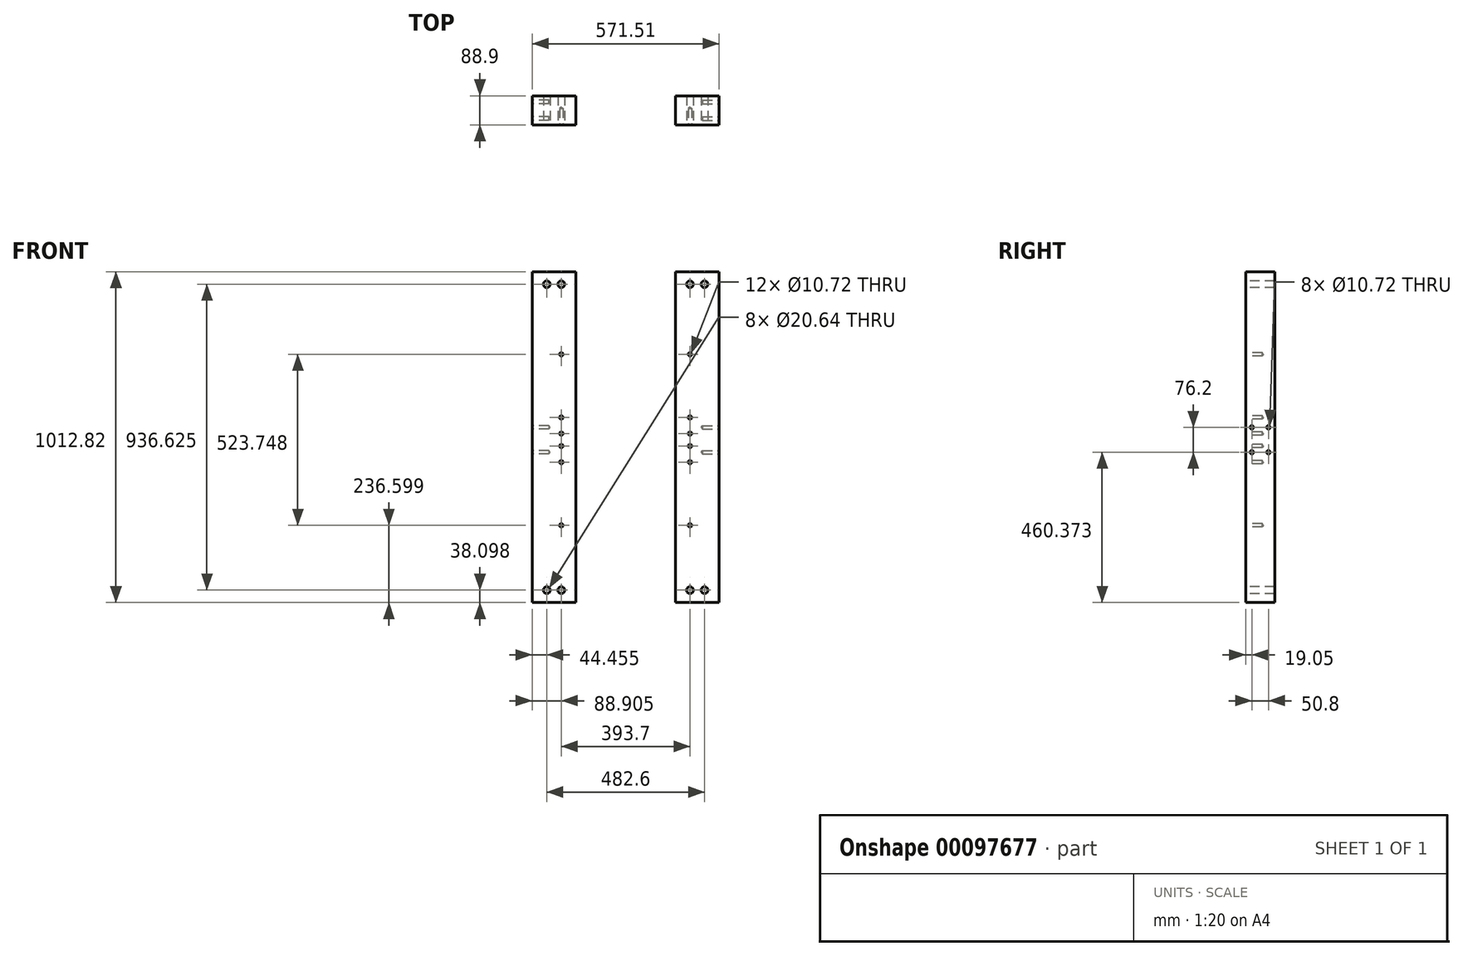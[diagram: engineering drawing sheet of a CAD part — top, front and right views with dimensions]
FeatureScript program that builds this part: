
annotation { "Feature Type Name" : "Feature", "Feature Type Description" : "" }
export const myFeature = defineFeature(function(context is Context, id is Id, definition is map)
    precondition{}
    {
        {
            var Q0;
            Q0=qCreatedBy(makeId("Top.planeOp"),FACE);
            var sketch = newSketch(context, id + "F0", { "sketchPlane" : qUnion([Q0])});
            skLineSegment(sketch, "E0.bottom", {"start": v(-66.68, 44.45) * mm, "end": v(66.68, 44.45) * mm});
            skLineSegment(sketch, "E0.top", {"start": v(-66.68, -44.45) * mm, "end": v(66.67, -44.45) * mm});
            skLineSegment(sketch, "E0.left", {"start": v(-66.67, 44.45) * mm, "end": v(-66.68, -44.45) * mm});
            skLineSegment(sketch, "E0.right", {"start": v(66.68, 44.45) * mm, "end": v(66.67, -44.45) * mm});
            skPoint(sketch, "E0.middle", {"position": v(0, 0) * mm});
            skSolve(sketch);
        }
        {
            var Q0;
            Q0=makeQuery(id+"F0.imprint","IMPRINT",FACE,{"disambiguationData":[TD([[makeQuery(id+"F0.imprint","IMPRINT",EDGE,{"derivedFrom":sQuery(id+"F0.wireOp",EDGE,"E0.bottom")}),-1.0]])]});
            extrude(context, id + "F1", {"entities" : qUnion([Q0]), "endBound" : BoundingType.SYMMETRIC, "depth" : 1012.82 * mm});
        }
        {
            var Q0;
            Q0=makeQuery(id+"F1.opExtrude","SWEPT_FACE",FACE,{"disambiguationData":[OSD([sQuery(id+"F0.wireOp",EDGE,"E0.top")])]});
            var sketch = newSketch(context, id + "F2", { "sketchPlane" : qUnion([Q0])});
            skLineSegment(sketch, "E1.0", {"start": v(-66.68, 506.41) * mm, "end": v(66.67, 506.41) * mm, "construction": true});
            skLineSegment(sketch, "E2.0", {"start": v(-66.68, -506.41) * mm, "end": v(66.67, -506.41) * mm, "construction": true});
            skLineSegment(sketch, "E3.0", {"start": v(-66.68, 506.41) * mm, "end": v(-66.68, -506.41) * mm, "construction": true});
            skLineSegment(sketch, "E4.0", {"start": v(-66.68, 468.31) * mm, "end": v(66.67, 468.31) * mm, "construction": true});
            skLineSegment(sketch, "E5.0", {"start": v(-66.68, -468.31) * mm, "end": v(66.67, -468.31) * mm, "construction": true});
            skLineSegment(sketch, "E6.0", {"start": v(-22.23, 506.41) * mm, "end": v(-22.23, -506.41) * mm, "construction": true});
            skLineSegment(sketch, "E7.0", {"start": v(22.22, 506.41) * mm, "end": v(22.22, -506.41) * mm, "construction": true});
            skLineSegment(sketch, "E8.0", {"start": v(-368.8, -7.94) * mm, "end": v(291.69, -7.94) * mm, "construction": true});
            skLineSegment(sketch, "E9.0", {"start": v(-368.8, 157.16) * mm, "end": v(291.69, 157.16) * mm, "construction": true});
            skLineSegment(sketch, "E10.0", {"start": v(-368.8, 253.94) * mm, "end": v(291.69, 253.94) * mm, "construction": true});
            skLineSegment(sketch, "E11.MirrorCS", {"start": v(-368.8, 60.39) * mm, "end": v(291.69, 60.39) * mm, "construction": true});
            skPoint(sketch, "E12", {"position": v(-22.23, 468.31) * mm});
            skPoint(sketch, "E13", {"position": v(22.22, 468.31) * mm});
            skPoint(sketch, "E14", {"position": v(22.22, 253.94) * mm});
            skPoint(sketch, "E15", {"position": v(22.22, 60.39) * mm});
            skPoint(sketch, "E16", {"position": v(-22.23, -468.31) * mm});
            skPoint(sketch, "E17", {"position": v(22.22, -468.31) * mm});
            skPoint(sketch, "E18.MirrorP", {"position": v(22.22, -76.26) * mm});
            skPoint(sketch, "E19.MirrorP", {"position": v(22.22, -269.81) * mm});
            skSolve(sketch);
        }
        {
            var Q0;
            Q0=sQuery(id+"F2.wireOp",VERTEX,"E12");
            var Q1;
            Q1=sQuery(id+"F2.wireOp",VERTEX,"E13");
            var Q2;
            Q2=sQuery(id+"F2.wireOp",VERTEX,"E17");
            var Q3;
            Q3=sQuery(id+"F2.wireOp",VERTEX,"E16");
            var Q4;
            Q4=makeQuery(id+"F1.opExtrude","SWEPT_BODY",BODY,{"disambiguationData":[OSD([sQuery(id+"F0.wireOp",EDGE,"E0.bottom"),sQuery(id+"F0.wireOp",EDGE,"E0.top"),sQuery(id+"F0.wireOp",EDGE,"E0.left"),sQuery(id+"F0.wireOp",EDGE,"E0.right")])]});
            hole(context, id + "F3", {"style" : HoleStyle.SIMPLE, "endStyle" : HoleEndStyle.THROUGH, "holeDiameter" : 20.64 * mm, "locations" : qUnion([Q0, Q1, Q2, Q3]), "scope" : qUnion([Q4]), "isTappedThrough" : true});
        }
        {
            var Q0;
            Q0=sQuery(id+"F2.wireOp",VERTEX,"E14");
            var Q1;
            Q1=sQuery(id+"F2.wireOp",VERTEX,"E15");
            var Q2;
            Q2=sQuery(id+"F2.wireOp",VERTEX,"E18.MirrorP");
            var Q3;
            Q3=sQuery(id+"F2.wireOp",VERTEX,"E19.MirrorP");
            var Q4;
            Q4=makeQuery(id+"F1.opExtrude","SWEPT_BODY",BODY,{"disambiguationData":[OSD([sQuery(id+"F0.wireOp",EDGE,"E0.bottom"),sQuery(id+"F0.wireOp",EDGE,"E0.top"),sQuery(id+"F0.wireOp",EDGE,"E0.left"),sQuery(id+"F0.wireOp",EDGE,"E0.right")])]});
            hole(context, id + "F4", {"style" : HoleStyle.SIMPLE, "endStyle" : HoleEndStyle.BLIND, "standardTappedOrClearance" : lookupTablePath({ "standard" : "ANSI", "engagement" : "75%", "pitch" : "13 tpi", "size" : "1/2", "type" : "Tapped" }), "standardBlindInLast" : lookupTablePath({ "standard" : "ANSI", "engagement" : "75%", "pitch" : "13 tpi", "size" : "1/2", "type" : "Tapped" }), "holeDiameter" : 10.72 * mm, "holeDepth" : 50.8 * mm, "locations" : qUnion([Q0, Q1, Q2, Q3]), "scope" : qUnion([Q4]), "majorDiameter" : 12.7 * mm});
        }
        {
            var Q0;
            {var subQ0=sQuery(id+"F0.wireOp",EDGE,"E0.top");Q0=makeQuery(id+"F2.imprint","IMPRINT",FACE,{"disambiguationData":[TD([[makeQuery(id+"F2.imprint","IMPRINT",EDGE,{"derivedFrom":makeQuery(id+"F1.opExtrude","CAP_EDGE",EDGE,{"disambiguationData":[OSD([subQ0])],"isStart":true})}),1.0]])]});}
            var sketch = newSketch(context, id + "F5", { "sketchPlane" : qUnion([Q0])});
            skLineSegment(sketch, "E20.0", {"start": v(-368.8, -7.94) * mm, "end": v(291.69, -7.94) * mm, "construction": true});
            skLineSegment(sketch, "E21.0", {"start": v(22.22, 506.41) * mm, "end": v(22.22, -506.41) * mm, "construction": true});
            skLineSegment(sketch, "E22.0", {"start": v(-368.8, 11.11) * mm, "end": v(291.69, 11.11) * mm, "construction": true});
            skPoint(sketch, "E23", {"position": v(22.22, 11.11) * mm});
            skPoint(sketch, "E24.MirrorP", {"position": v(22.22, -26.99) * mm});
            skSolve(sketch);
        }
        {
            var Q0;
            Q0=sQuery(id+"F5.wireOp",VERTEX,"E23");
            var Q1;
            Q1=sQuery(id+"F5.wireOp",VERTEX,"E24.MirrorP");
            var Q2;
            Q2=makeQuery(id+"F1.opExtrude","SWEPT_BODY",BODY,{"disambiguationData":[OSD([sQuery(id+"F0.wireOp",EDGE,"E0.bottom"),sQuery(id+"F0.wireOp",EDGE,"E0.top"),sQuery(id+"F0.wireOp",EDGE,"E0.left"),sQuery(id+"F0.wireOp",EDGE,"E0.right")])]});
            hole(context, id + "F6", {"style" : HoleStyle.SIMPLE, "endStyle" : HoleEndStyle.BLIND, "standardTappedOrClearance" : lookupTablePath({ "standard" : "ANSI", "engagement" : "75%", "pitch" : "13 tpi", "size" : "1/2", "type" : "Tapped" }), "standardBlindInLast" : lookupTablePath({ "standard" : "ANSI", "engagement" : "75%", "pitch" : "13 tpi", "size" : "1/2", "type" : "Tapped" }), "holeDiameter" : 10.72 * mm, "holeDepth" : 50.8 * mm, "locations" : qUnion([Q0, Q1]), "scope" : qUnion([Q2]), "majorDiameter" : 12.7 * mm});
        }
        {
            var Q0;
            Q0=makeQuery(id+"F1.opExtrude","SWEPT_FACE",FACE,{"disambiguationData":[OSD([sQuery(id+"F0.wireOp",EDGE,"E0.left")])]});
            var sketch = newSketch(context, id + "F7", { "sketchPlane" : qUnion([Q0])});
            skLineSegment(sketch, "E25.0", {"start": v(-44.45, -7.94) * mm, "end": v(44.45, -7.94) * mm, "construction": true});
            skLineSegment(sketch, "E26", {"start": v(0, 506.41) * mm, "end": v(0, -506.41) * mm, "construction": true});
            skLineSegment(sketch, "E27.0", {"start": v(-44.45, 30.16) * mm, "end": v(44.45, 30.16) * mm, "construction": true});
            skLineSegment(sketch, "E28.0", {"start": v(-25.4, 506.41) * mm, "end": v(-25.4, -506.41) * mm, "construction": true});
            skPoint(sketch, "E29", {"position": v(-25.4, 30.16) * mm});
            skPoint(sketch, "E30.0.1.0", {"position": v(-25.4, -46.04) * mm});
            skPoint(sketch, "E30.1.0.0", {"position": v(25.4, 30.16) * mm});
            skPoint(sketch, "E30.1.1.0", {"position": v(25.4, -46.04) * mm});
            skLineSegment(sketch, "E30.direction1", {"start": v(-25.4, 30.16) * mm, "end": v(25.4, 30.16) * mm, "construction": true});
            skLineSegment(sketch, "E30.direction2", {"start": v(-25.4, 30.16) * mm, "end": v(-25.4, -46.04) * mm, "construction": true});
            skSolve(sketch);
        }
        {
            var Q0;
            Q0=sQuery(id+"F7.wireOp",VERTEX,"E29");
            var Q1;
            Q1=sQuery(id+"F7.wireOp",VERTEX,"E30.1.0.0");
            var Q2;
            Q2=sQuery(id+"F7.wireOp",VERTEX,"E30.0.1.0");
            var Q3;
            Q3=sQuery(id+"F7.wireOp",VERTEX,"E30.1.1.0");
            var Q4;
            Q4=makeQuery(id+"F1.opExtrude","SWEPT_BODY",BODY,{"disambiguationData":[OSD([sQuery(id+"F0.wireOp",EDGE,"E0.bottom"),sQuery(id+"F0.wireOp",EDGE,"E0.top"),sQuery(id+"F0.wireOp",EDGE,"E0.left"),sQuery(id+"F0.wireOp",EDGE,"E0.right")])]});
            hole(context, id + "F8", {"style" : HoleStyle.SIMPLE, "endStyle" : HoleEndStyle.BLIND, "standardTappedOrClearance" : lookupTablePath({ "standard" : "ANSI", "engagement" : "75%", "pitch" : "13 tpi", "size" : "1/2", "type" : "Tapped" }), "standardBlindInLast" : lookupTablePath({ "standard" : "ANSI", "engagement" : "75%", "pitch" : "13 tpi", "size" : "1/2", "type" : "Tapped" }), "holeDiameter" : 10.72 * mm, "holeDepth" : 50.8 * mm, "locations" : qUnion([Q0, Q1, Q2, Q3]), "scope" : qUnion([Q4]), "majorDiameter" : 12.7 * mm});
        }
        {
            var Q0;
            Q0=makeQuery(id+"F1.opExtrude","SWEPT_FACE",FACE,{"disambiguationData":[OSD([sQuery(id+"F0.wireOp",EDGE,"E0.right")])]});
            cPlane(context, id + "F9", {"entities" : qUnion([Q0]), "cplaneType" : CPlaneType.OFFSET, "offset" : 152.4 * mm, "width" : 152.4 * mm, "height" : 152.4 * mm});
        }
        {
            var Q0;
            Q0=makeQuery(id+"F1.opExtrude","SWEPT_BODY",BODY,{"disambiguationData":[OSD([sQuery(id+"F0.wireOp",EDGE,"E0.bottom"),sQuery(id+"F0.wireOp",EDGE,"E0.top"),sQuery(id+"F0.wireOp",EDGE,"E0.left"),sQuery(id+"F0.wireOp",EDGE,"E0.right")])]});
            var Q1;
            Q1=qCreatedBy(id+"F9.planeOp",FACE);
            mirror(context, id + "F10", {"entities" : qUnion([Q0]), "mirrorPlane" : qUnion([Q1])});
        }
    });
